# Revit family: KM2.101
name_source: partatom
category: Plumbing Fixtures
revit_build: Autodesk Revit Architecture 2012 (Build: 20110309_2315(x64)
units: mm (PartAtom-declared; Revit-internal decimal feet)

## types (1)
- KM2.101
    Assembly Code = D2010
    CW Connection = Yes
    CWFU = 0
    Cartridge assembly = C-KM9.200
    Cartridge repair kit = C-KM9.290
    Cost = 0 $
    Delault Elevation = 0' - 0"
    Description = Self closing. Non hold open. Flow controller. Flow cycle 1-20 secs. 1/2" MI
    HW Connection = No
    HWFU = 0
    Keynote = The reduced flow rate enables smaller supply pipes to be used with a subsequent saving in installation material costs
    Manufacturer = COBRA
    Material = Chrome - Brushed
    Model = KM2.101
    Range = Metering Valves
    Type Comments = SANS 1808-9
    URL = http://www.cobra.co.za
    Vent Connection = No
    WFU = 0
    Waste Connection = No

## geometry (parser evidence)
native form markers: Blend x3
no freeform markers — native parametric forms only
